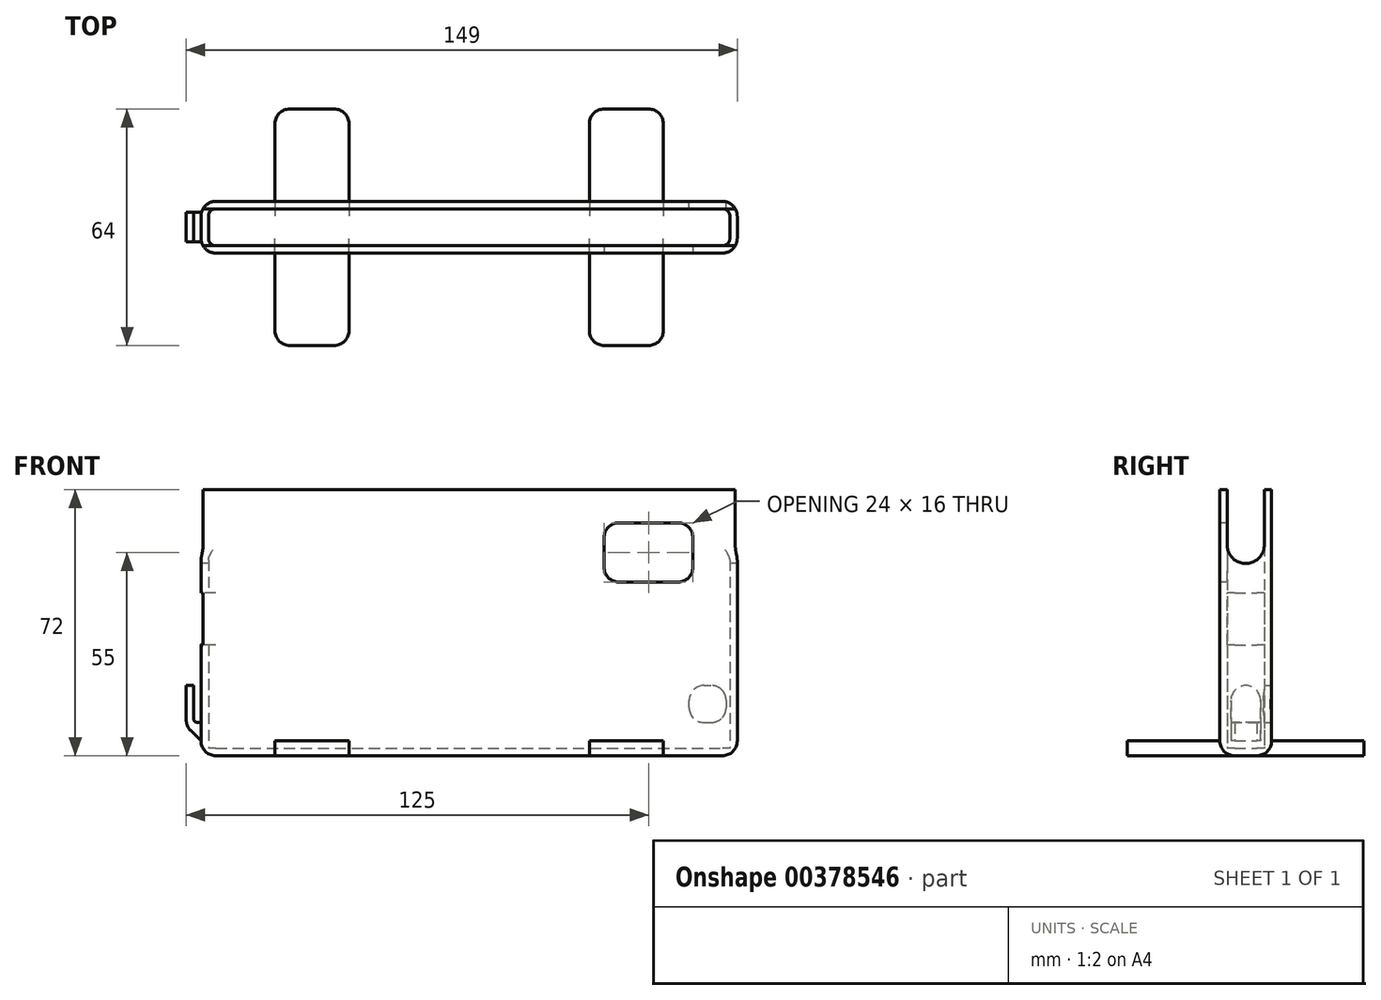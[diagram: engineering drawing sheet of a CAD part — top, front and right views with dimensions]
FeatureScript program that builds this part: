
annotation { "Feature Type Name" : "Feature", "Feature Type Description" : "" }
export const myFeature = defineFeature(function(context is Context, id is Id, definition is map)
    precondition{}
    {
        {
            var Q0;
            Q0=qCreatedBy(makeId("Top.planeOp"),FACE);
            var sketch = newSketch(context, id + "F0", { "sketchPlane" : qUnion([Q0])});
            skLineSegment(sketch, "E0.bottom", {"start": v(0, 0) * mm, "end": v(145, 0) * mm});
            skLineSegment(sketch, "E0.top", {"start": v(0, 14) * mm, "end": v(145, 14) * mm});
            skLineSegment(sketch, "E0.left", {"start": v(0, 0) * mm, "end": v(0, 14) * mm});
            skLineSegment(sketch, "E0.right", {"start": v(145, 0) * mm, "end": v(145, 14) * mm});
            skSolve(sketch);
        }
        {
            var Q0;
            Q0=qSketchRegion(id+"F0",true);
            extrude(context, id + "F1", {"entities" : qUnion([Q0]), "depth" : 2 * mm});
        }
        {
            var Q0;
            Q0=makeQuery(id+"F1.opExtrude","CAP_FACE",FACE,{"disambiguationData":[OSD([sQuery(id+"F0.wireOp",EDGE,"E0.bottom"),sQuery(id+"F0.wireOp",EDGE,"E0.top"),sQuery(id+"F0.wireOp",EDGE,"E0.left"),sQuery(id+"F0.wireOp",EDGE,"E0.right")])],"isStart":false});
            var sketch = newSketch(context, id + "F2", { "sketchPlane" : qUnion([Q0])});
            skLineSegment(sketch, "E1.0", {"start": v(0, 14) * mm, "end": v(145, 14) * mm});
            skLineSegment(sketch, "E1.1", {"start": v(0, 0) * mm, "end": v(0, 14) * mm});
            skLineSegment(sketch, "E1.2", {"start": v(0, 0) * mm, "end": v(145, 0) * mm});
            skLineSegment(sketch, "E1.3", {"start": v(145, 0) * mm, "end": v(145, 14) * mm});
            skLineSegment(sketch, "E2.0", {"start": v(2, 12) * mm, "end": v(143, 12) * mm});
            skLineSegment(sketch, "E2.1", {"start": v(2, 2) * mm, "end": v(2, 12) * mm});
            skLineSegment(sketch, "E2.2", {"start": v(2, 2) * mm, "end": v(143, 2) * mm});
            skLineSegment(sketch, "E2.3", {"start": v(143, 2) * mm, "end": v(143, 12) * mm});
            skSolve(sketch);
        }
        {
            var Q0;
            Q0=qSketchRegion(id+"F2",true);
            extrude(context, id + "F3", {"entities" : qUnion([Q0]), "operationType" : NewBodyOperationType.ADD, "depth" : 70 * mm});
        }
        {
            var Q0;
            Q0=makeQuery(id+"F3.opExtrude","SWEPT_EDGE",EDGE,{"disambiguationData":[OSD([sQuery(id+"F2.wireOp",EDGE,"E2.1"),sQuery(id+"F2.wireOp",EDGE,"E2.2")])]});
            var Q1;
            Q1=makeQuery(id+"F3.opExtrude","SWEPT_EDGE",EDGE,{"disambiguationData":[OSD([sQuery(id+"F2.wireOp",EDGE,"E2.0"),sQuery(id+"F2.wireOp",EDGE,"E2.1")])]});
            var Q2;
            Q2=makeQuery(id+"F3.opExtrude","SWEPT_EDGE",EDGE,{"disambiguationData":[OSD([sQuery(id+"F2.wireOp",EDGE,"E2.0"),sQuery(id+"F2.wireOp",EDGE,"E2.3")])]});
            var Q3;
            Q3=makeQuery(id+"F3.opExtrude","SWEPT_EDGE",EDGE,{"disambiguationData":[OSD([sQuery(id+"F2.wireOp",EDGE,"E2.2"),sQuery(id+"F2.wireOp",EDGE,"E2.3")])]});
            var Q4;
            Q4=makeQuery(id+"F3.opExtrude","CAP_EDGE",EDGE,{"disambiguationData":[OSD([sQuery(id+"F2.wireOp",EDGE,"E2.2")])],"isStart":true});
            var Q5;
            Q5=makeQuery(id+"F3.opExtrude","CAP_EDGE",EDGE,{"disambiguationData":[OSD([sQuery(id+"F2.wireOp",EDGE,"E2.3")])],"isStart":true});
            var Q6;
            Q6=makeQuery(id+"F3.opExtrude","CAP_EDGE",EDGE,{"disambiguationData":[OSD([sQuery(id+"F2.wireOp",EDGE,"E2.0")])],"isStart":true});
            var Q7;
            Q7=makeQuery(id+"F3.opExtrude","CAP_EDGE",EDGE,{"disambiguationData":[OSD([sQuery(id+"F2.wireOp",EDGE,"E2.1")])],"isStart":true});
            fillet(context, id + "F4", {"entities" : qUnion([Q0, Q1, Q2, Q3, Q4, Q5, Q6, Q7]), "radius" : 2 * mm, "tangentPropagation" : true, "allowEdgeOverflow" : false});
        }
        {
            var Q0;
            Q0=makeQuery(id+"F3.boolean.opBoolean","MERGE",EDGE,{"derivedFrom":[makeQuery(id+"F1.opExtrude","SWEPT_EDGE",EDGE,{"disambiguationData":[OSD([sQuery(id+"F0.wireOp",EDGE,"E0.bottom"),sQuery(id+"F0.wireOp",EDGE,"E0.left")])]}),makeQuery(id+"F3.opExtrude","SWEPT_EDGE",EDGE,{"disambiguationData":[OSD([sQuery(id+"F2.wireOp",EDGE,"E1.1"),sQuery(id+"F2.wireOp",EDGE,"E1.2")])]})]});
            var Q1;
            Q1=makeQuery(id+"F3.boolean.opBoolean","MERGE",EDGE,{"derivedFrom":[makeQuery(id+"F1.opExtrude","SWEPT_EDGE",EDGE,{"disambiguationData":[OSD([sQuery(id+"F0.wireOp",EDGE,"E0.top"),sQuery(id+"F0.wireOp",EDGE,"E0.left")])]}),makeQuery(id+"F3.opExtrude","SWEPT_EDGE",EDGE,{"disambiguationData":[OSD([sQuery(id+"F2.wireOp",EDGE,"E1.0"),sQuery(id+"F2.wireOp",EDGE,"E1.1")])]})]});
            var Q2;
            Q2=makeQuery(id+"F3.boolean.opBoolean","MERGE",EDGE,{"derivedFrom":[makeQuery(id+"F1.opExtrude","SWEPT_EDGE",EDGE,{"disambiguationData":[OSD([sQuery(id+"F0.wireOp",EDGE,"E0.top"),sQuery(id+"F0.wireOp",EDGE,"E0.right")])]}),makeQuery(id+"F3.opExtrude","SWEPT_EDGE",EDGE,{"disambiguationData":[OSD([sQuery(id+"F2.wireOp",EDGE,"E1.0"),sQuery(id+"F2.wireOp",EDGE,"E1.3")])]})]});
            var Q3;
            Q3=makeQuery(id+"F3.boolean.opBoolean","MERGE",EDGE,{"derivedFrom":[makeQuery(id+"F1.opExtrude","SWEPT_EDGE",EDGE,{"disambiguationData":[OSD([sQuery(id+"F0.wireOp",EDGE,"E0.bottom"),sQuery(id+"F0.wireOp",EDGE,"E0.right")])]}),makeQuery(id+"F3.opExtrude","SWEPT_EDGE",EDGE,{"disambiguationData":[OSD([sQuery(id+"F2.wireOp",EDGE,"E1.2"),sQuery(id+"F2.wireOp",EDGE,"E1.3")])]})]});
            var Q4;
            Q4=makeQuery(id+"F1.opExtrude","CAP_EDGE",EDGE,{"disambiguationData":[OSD([sQuery(id+"F0.wireOp",EDGE,"E0.bottom")])],"isStart":true});
            var Q5;
            Q5=makeQuery(id+"F1.opExtrude","CAP_EDGE",EDGE,{"disambiguationData":[OSD([sQuery(id+"F0.wireOp",EDGE,"E0.left")])],"isStart":true});
            var Q6;
            Q6=makeQuery(id+"F1.opExtrude","CAP_EDGE",EDGE,{"disambiguationData":[OSD([sQuery(id+"F0.wireOp",EDGE,"E0.top")])],"isStart":true});
            var Q7;
            Q7=makeQuery(id+"F1.opExtrude","CAP_EDGE",EDGE,{"disambiguationData":[OSD([sQuery(id+"F0.wireOp",EDGE,"E0.right")])],"isStart":true});
            fillet(context, id + "F5", {"entities" : qUnion([Q0, Q1, Q2, Q3, Q4, Q5, Q6, Q7]), "radius" : 4 * mm, "tangentPropagation" : true, "allowEdgeOverflow" : false});
        }
        {
            var Q0;
            Q0=makeQuery(id+"F3.boolean.opBoolean","MERGE",FACE,{"derivedFrom":[makeQuery(id+"F1.opExtrude","SWEPT_FACE",FACE,{"disambiguationData":[OSD([sQuery(id+"F0.wireOp",EDGE,"E0.left")])]}),makeQuery(id+"F3.opExtrude","SWEPT_FACE",FACE,{"disambiguationData":[OSD([sQuery(id+"F2.wireOp",EDGE,"E1.1")])]})]});
            var sketch = newSketch(context, id + "F6", { "sketchPlane" : qUnion([Q0])});
            skLineSegment(sketch, "E3", {"start": v(-7, 72) * mm, "end": v(-7, 57) * mm, "construction": true});
            skArc(sketch, "E4.0.startCap", {"start": v(-12, 72) * mm, "mid": v(-7, 77) * mm, "end": v(-2, 72) * mm});
            skArc(sketch, "E4.0.endCap", {"start": v(-2, 57) * mm, "mid": v(-7, 52) * mm, "end": v(-12, 57) * mm});
            skLineSegment(sketch, "E4.0.left", {"start": v(-2, 72) * mm, "end": v(-2, 57) * mm});
            skLineSegment(sketch, "E4.0.right", {"start": v(-12, 72) * mm, "end": v(-12, 57) * mm});
            skSolve(sketch);
        }
        {
            var Q0;
            Q0=qSketchRegion(id+"F6",true);
            extrude(context, id + "F7", {"entities" : qUnion([Q0]), "operationType" : NewBodyOperationType.REMOVE, "endBound" : BoundingType.THROUGH_ALL, "oppositeDirection" : true, "depth" : 25 * mm});
        }
        {
            var Q0;
            Q0=makeQuery(id+"F3.boolean.opBoolean","MERGE",FACE,{"derivedFrom":[makeQuery(id+"F1.opExtrude","SWEPT_FACE",FACE,{"disambiguationData":[OSD([sQuery(id+"F0.wireOp",EDGE,"E0.bottom")])]}),makeQuery(id+"F3.opExtrude","SWEPT_FACE",FACE,{"disambiguationData":[OSD([sQuery(id+"F2.wireOp",EDGE,"E1.2")])]})]});
            var sketch = newSketch(context, id + "F8", { "sketchPlane" : qUnion([Q0])});
            skLineSegment(sketch, "E5.bottom", {"start": v(113, 63) * mm, "end": v(129, 63) * mm});
            skLineSegment(sketch, "E5.top", {"start": v(113, 47) * mm, "end": v(129, 47) * mm});
            skLineSegment(sketch, "E5.left", {"start": v(109, 59) * mm, "end": v(109, 51) * mm});
            skLineSegment(sketch, "E5.right", {"start": v(133, 59) * mm, "end": v(133, 51) * mm});
            skPoint(sketch, "E6", {"position": v(109, 55) * mm});
            skPoint(sketch, "E7.visualSharp", {"position": v(109, 63) * mm});
            skArc(sketch, "E7.filletArc", {"start": v(113, 63) * mm, "mid": v(110.17, 61.83) * mm, "end": v(109, 59) * mm});
            skPoint(sketch, "E8.visualSharp", {"position": v(133, 63) * mm});
            skArc(sketch, "E8.filletArc", {"start": v(133, 59) * mm, "mid": v(131.83, 61.83) * mm, "end": v(129, 63) * mm});
            skPoint(sketch, "E9.visualSharp", {"position": v(133, 47) * mm});
            skArc(sketch, "E9.filletArc", {"start": v(129, 47) * mm, "mid": v(131.83, 48.17) * mm, "end": v(133, 51) * mm});
            skPoint(sketch, "E10.visualSharp", {"position": v(109, 47) * mm});
            skArc(sketch, "E10.filletArc", {"start": v(109, 51) * mm, "mid": v(110.17, 48.17) * mm, "end": v(113, 47) * mm});
            skPoint(sketch, "E11", {"position": v(121, 63) * mm});
            skSolve(sketch);
        }
        {
            var Q0;
            Q0=qSketchRegion(id+"F8",true);
            extrude(context, id + "F9", {"entities" : qUnion([Q0]), "operationType" : NewBodyOperationType.REMOVE, "endBound" : BoundingType.UP_TO_NEXT, "oppositeDirection" : true, "depth" : 25 * mm});
        }
        {
            var Q0;
            Q0=makeQuery(id+"F3.boolean.opBoolean","MERGE",FACE,{"derivedFrom":[makeQuery(id+"F1.opExtrude","SWEPT_FACE",FACE,{"disambiguationData":[OSD([sQuery(id+"F0.wireOp",EDGE,"E0.left")])]}),makeQuery(id+"F3.opExtrude","SWEPT_FACE",FACE,{"disambiguationData":[OSD([sQuery(id+"F2.wireOp",EDGE,"E1.1")])]})]});
            var sketch = newSketch(context, id + "F10", { "sketchPlane" : qUnion([Q0])});
            skLineSegment(sketch, "E12.bottom", {"start": v(-11, 19) * mm, "end": v(-3, 19) * mm});
            skLineSegment(sketch, "E12.top", {"start": v(-11, 4) * mm, "end": v(-3, 4) * mm});
            skLineSegment(sketch, "E12.left", {"start": v(-11, 19) * mm, "end": v(-11, 4) * mm});
            skLineSegment(sketch, "E12.right", {"start": v(-3, 19) * mm, "end": v(-3, 4) * mm});
            skPoint(sketch, "E13", {"position": v(-7, 4) * mm});
            skSolve(sketch);
        }
        {
            var Q0;
            Q0=qSketchRegion(id+"F10",true);
            extrude(context, id + "F11", {"entities" : qUnion([Q0]), "operationType" : NewBodyOperationType.ADD, "depth" : 4 * mm});
        }
        {
            var Q0;
            Q0=makeQuery(id+"F11.opExtrude","CAP_EDGE",EDGE,{"disambiguationData":[OSD([sQuery(id+"F10.wireOp",EDGE,"E12.top")])],"isStart":false});
            chamfer(context, id + "F12", {"entities" : qUnion([Q0]), "width" : 4 * mm, "tangentPropagation" : true});
        }
        {
            var Q0;
            Q0=makeQuery(id+"F11.opExtrude","SWEPT_FACE",FACE,{"disambiguationData":[OSD([sQuery(id+"F10.wireOp",EDGE,"E12.bottom")])]});
            var sketch = newSketch(context, id + "F13", { "sketchPlane" : qUnion([Q0])});
            skLineSegment(sketch, "E14.bottom", {"start": v(-2, 11) * mm, "end": v(0, 11) * mm});
            skLineSegment(sketch, "E14.top", {"start": v(-2, 3) * mm, "end": v(0, 3) * mm});
            skLineSegment(sketch, "E14.left", {"start": v(0, 3) * mm, "end": v(0, 11) * mm});
            skLineSegment(sketch, "E14.right", {"start": v(-2, 3) * mm, "end": v(-2, 11) * mm});
            skSolve(sketch);
        }
        {
            var Q0;
            Q0=qSketchRegion(id+"F13",true);
            extrude(context, id + "F14", {"entities" : qUnion([Q0]), "operationType" : NewBodyOperationType.REMOVE, "oppositeDirection" : true, "depth" : 10 * mm});
        }
        {
            var Q0;
            Q0=makeQuery(id+"F11.opExtrude","SWEPT_EDGE",EDGE,{"disambiguationData":[OSD([sQuery(id+"F10.wireOp",EDGE,"E12.bottom"),sQuery(id+"F10.wireOp",EDGE,"E12.left")])]});
            var Q1;
            Q1=makeQuery(id+"F11.opExtrude","SWEPT_EDGE",EDGE,{"disambiguationData":[OSD([sQuery(id+"F10.wireOp",EDGE,"E12.bottom"),sQuery(id+"F10.wireOp",EDGE,"E12.right")])]});
            var Q2;
            {var subQ0=sQuery(id+"F10.wireOp",EDGE,"E12.top");Q2=makeQuery(id+"F12.opChamfer","BLEND_EDGE",EDGE,{"blendedFrom":[makeQuery(id+"F11.opExtrude","CAP_EDGE",EDGE,{"disambiguationData":[OSD([subQ0])],"isStart":false}),makeQuery(id+"F11.opExtrude","CAP_FACE",FACE,{"disambiguationData":[OSD([sQuery(id+"F10.wireOp",EDGE,"E12.bottom"),subQ0,sQuery(id+"F10.wireOp",EDGE,"E12.left"),sQuery(id+"F10.wireOp",EDGE,"E12.right")])],"isStart":false})],"blendedInto":[makeQuery(id+"F11.opExtrude","CAP_FACE",FACE,{"disambiguationData":[OSD([sQuery(id+"F10.wireOp",EDGE,"E12.bottom"),subQ0,sQuery(id+"F10.wireOp",EDGE,"E12.left"),sQuery(id+"F10.wireOp",EDGE,"E12.right")])],"isStart":false})]});}
            fillet(context, id + "F15", {"entities" : qUnion([Q0, Q1, Q2]), "radius" : 4 * mm, "tangentPropagation" : true, "allowEdgeOverflow" : false});
        }
        {
            var Q0;
            Q0=makeQuery(id+"F14.boolean.opBoolean","COPY",EDGE,{"derivedFrom":makeQuery(id+"F14.opExtrude","CAP_EDGE",EDGE,{"disambiguationData":[OSD([sQuery(id+"F13.wireOp",EDGE,"E14.right")])],"isStart":false})});
            fillet(context, id + "F16", {"entities" : qUnion([Q0]), "radius" : 1 * mm, "tangentPropagation" : true, "allowEdgeOverflow" : false});
        }
        {
            var Q0;
            Q0=makeQuery(id+"F3.boolean.opBoolean","MERGE",FACE,{"derivedFrom":[makeQuery(id+"F1.opExtrude","SWEPT_FACE",FACE,{"disambiguationData":[OSD([sQuery(id+"F0.wireOp",EDGE,"E0.top")])]}),makeQuery(id+"F3.opExtrude","SWEPT_FACE",FACE,{"disambiguationData":[OSD([sQuery(id+"F2.wireOp",EDGE,"E1.0")])]})]});
            var sketch = newSketch(context, id + "F17", { "sketchPlane" : qUnion([Q0])});
            skLineSegment(sketch, "E15.bottom", {"start": v(-138, 19) * mm, "end": v(-136, 19) * mm});
            skLineSegment(sketch, "E15.top", {"start": v(-138, 9) * mm, "end": v(-136, 9) * mm});
            skLineSegment(sketch, "E15.left", {"start": v(-142, 15) * mm, "end": v(-142, 13) * mm});
            skLineSegment(sketch, "E15.right", {"start": v(-132, 15) * mm, "end": v(-132, 13) * mm});
            skPoint(sketch, "E16.visualSharp", {"position": v(-142, 19) * mm});
            skArc(sketch, "E16.filletArc", {"start": v(-138, 19) * mm, "mid": v(-140.83, 17.83) * mm, "end": v(-142, 15) * mm});
            skPoint(sketch, "E17.visualSharp", {"position": v(-132, 19) * mm});
            skArc(sketch, "E17.filletArc", {"start": v(-132, 15) * mm, "mid": v(-133.17, 17.83) * mm, "end": v(-136, 19) * mm});
            skPoint(sketch, "E18.visualSharp", {"position": v(-132, 9) * mm});
            skArc(sketch, "E18.filletArc", {"start": v(-136, 9) * mm, "mid": v(-133.17, 10.17) * mm, "end": v(-132, 13) * mm});
            skPoint(sketch, "E19.visualSharp", {"position": v(-142, 9) * mm});
            skArc(sketch, "E19.filletArc", {"start": v(-142, 13) * mm, "mid": v(-140.83, 10.17) * mm, "end": v(-138, 9) * mm});
            skPoint(sketch, "E20", {"position": v(-137, 19) * mm});
            skPoint(sketch, "E21", {"position": v(-132, 14) * mm});
            skSolve(sketch);
        }
        {
            var Q0;
            Q0=qSketchRegion(id+"F17",true);
            extrude(context, id + "F18", {"entities" : qUnion([Q0]), "operationType" : NewBodyOperationType.REMOVE, "endBound" : BoundingType.UP_TO_NEXT, "oppositeDirection" : true, "depth" : 25 * mm});
        }
        {
            var Q0;
            Q0=makeQuery(id+"F3.boolean.opBoolean","MERGE",FACE,{"derivedFrom":[makeQuery(id+"F1.opExtrude","SWEPT_FACE",FACE,{"disambiguationData":[OSD([sQuery(id+"F0.wireOp",EDGE,"E0.left")])]}),makeQuery(id+"F3.opExtrude","SWEPT_FACE",FACE,{"disambiguationData":[OSD([sQuery(id+"F2.wireOp",EDGE,"E1.1")])]})]});
            var sketch = newSketch(context, id + "F19", { "sketchPlane" : qUnion([Q0])});
            skLineSegment(sketch, "E22.bottom", {"start": v(-2, 44) * mm, "end": v(-12, 44) * mm});
            skLineSegment(sketch, "E22.top", {"start": v(-2, 30) * mm, "end": v(-12, 30) * mm});
            skLineSegment(sketch, "E22.left", {"start": v(-2, 44) * mm, "end": v(-2, 30) * mm});
            skLineSegment(sketch, "E22.right", {"start": v(-12, 44) * mm, "end": v(-12, 30) * mm});
            skPoint(sketch, "E22.middle", {"position": v(-7, 37) * mm});
            skLineSegment(sketch, "E23", {"start": v(-10, 31) * mm, "end": v(-4, 31) * mm, "construction": true});
            skPoint(sketch, "E24", {"position": v(-7, 31) * mm});
            skSolve(sketch);
        }
        {
            var Q0;
            Q0=qSketchRegion(id+"F19",true);
            extrude(context, id + "F20", {"entities" : qUnion([Q0]), "operationType" : NewBodyOperationType.REMOVE, "endBound" : BoundingType.UP_TO_NEXT, "oppositeDirection" : true, "depth" : 25 * mm});
        }
        {
            var Q0;
            Q0=makeQuery(id+"F3.boolean.opBoolean","MERGE",FACE,{"derivedFrom":[makeQuery(id+"F1.opExtrude","SWEPT_FACE",FACE,{"disambiguationData":[OSD([sQuery(id+"F0.wireOp",EDGE,"E0.top")])]}),makeQuery(id+"F3.opExtrude","SWEPT_FACE",FACE,{"disambiguationData":[OSD([sQuery(id+"F2.wireOp",EDGE,"E1.0")])]})]});
            var sketch = newSketch(context, id + "F21", { "sketchPlane" : qUnion([Q0])});
            skLineSegment(sketch, "E25.bottom", {"start": v(-125, 4) * mm, "end": v(-105, 4) * mm});
            skLineSegment(sketch, "E25.top", {"start": v(-125, 0) * mm, "end": v(-105, 0) * mm});
            skLineSegment(sketch, "E25.left", {"start": v(-125, 4) * mm, "end": v(-125, 0) * mm});
            skLineSegment(sketch, "E25.right", {"start": v(-105, 4) * mm, "end": v(-105, 0) * mm});
            skLineSegment(sketch, "E26.bottom", {"start": v(-40, 4) * mm, "end": v(-20, 4) * mm});
            skLineSegment(sketch, "E26.top", {"start": v(-40, 0) * mm, "end": v(-20, 0) * mm});
            skLineSegment(sketch, "E26.left", {"start": v(-40, 4) * mm, "end": v(-40, 0) * mm});
            skLineSegment(sketch, "E26.right", {"start": v(-20, 4) * mm, "end": v(-20, 0) * mm});
            skSolve(sketch);
        }
        {
            var Q0;
            Q0=qSketchRegion(id+"F21",true);
            var Q1;
            Q1=makeQuery(id+"F1.opExtrude","SWEPT_BODY",BODY,{"disambiguationData":[OSD([sQuery(id+"F0.wireOp",EDGE,"E0.bottom"),sQuery(id+"F0.wireOp",EDGE,"E0.top"),sQuery(id+"F0.wireOp",EDGE,"E0.left"),sQuery(id+"F0.wireOp",EDGE,"E0.right")])]});
            extrude(context, id + "F22", {"entities" : qUnion([Q0]), "operationType" : NewBodyOperationType.ADD, "depth" : 25 * mm, "hasSecondDirection" : true, "secondDirectionBound" : SecondDirectionBoundingType.UP_TO_BODY, "secondDirectionOppositeDirection" : true, "secondDirectionBoundEntityBody" : qUnion([Q1]), "secondDirectionDepth" : 25 * mm});
        }
        {
            var Q0;
            Q0=makeQuery(id+"F3.boolean.opBoolean","MERGE",FACE,{"derivedFrom":[makeQuery(id+"F1.opExtrude","SWEPT_FACE",FACE,{"disambiguationData":[OSD([sQuery(id+"F0.wireOp",EDGE,"E0.bottom")])]}),makeQuery(id+"F3.opExtrude","SWEPT_FACE",FACE,{"disambiguationData":[OSD([sQuery(id+"F2.wireOp",EDGE,"E1.2")])]})]});
            var sketch = newSketch(context, id + "F23", { "sketchPlane" : qUnion([Q0])});
            skLineSegment(sketch, "E27.bottom", {"start": v(20, 4) * mm, "end": v(40, 4) * mm});
            skLineSegment(sketch, "E27.top", {"start": v(20, 0) * mm, "end": v(40, 0) * mm});
            skLineSegment(sketch, "E27.left", {"start": v(20, 4) * mm, "end": v(20, 0) * mm});
            skLineSegment(sketch, "E27.right", {"start": v(40, 4) * mm, "end": v(40, 0) * mm});
            skLineSegment(sketch, "E28.bottom", {"start": v(105, 4) * mm, "end": v(125, 4) * mm});
            skLineSegment(sketch, "E28.top", {"start": v(105, 0) * mm, "end": v(125, 0) * mm});
            skLineSegment(sketch, "E28.left", {"start": v(105, 4) * mm, "end": v(105, 0) * mm});
            skLineSegment(sketch, "E28.right", {"start": v(125, 4) * mm, "end": v(125, 0) * mm});
            skSolve(sketch);
        }
        {
            var Q0;
            Q0=qSketchRegion(id+"F23",true);
            var Q1;
            Q1=makeQuery(id+"F1.opExtrude","SWEPT_BODY",BODY,{"disambiguationData":[OSD([sQuery(id+"F0.wireOp",EDGE,"E0.bottom"),sQuery(id+"F0.wireOp",EDGE,"E0.top"),sQuery(id+"F0.wireOp",EDGE,"E0.left"),sQuery(id+"F0.wireOp",EDGE,"E0.right")])]});
            extrude(context, id + "F24", {"entities" : qUnion([Q0]), "operationType" : NewBodyOperationType.ADD, "depth" : 25 * mm, "hasSecondDirection" : true, "secondDirectionBound" : SecondDirectionBoundingType.UP_TO_BODY, "secondDirectionOppositeDirection" : true, "secondDirectionBoundEntityBody" : qUnion([Q1]), "secondDirectionDepth" : 25 * mm});
        }
        {
            var Q0;
            {var subQ0=sQuery(id+"F23.wireOp",EDGE,"E27.left");Q0=makeQuery(id+"F24.opExtrude","CAP_EDGE",EDGE,{"disambiguationData":[OSD([subQ0]),topologyDisambiguationEdgeConnected([makeQuery(id+"F23.imprint","IMPRINT",EDGE,{"derivedFrom":sQuery(id+"F23.wireOp",EDGE,"E27.bottom")})])],"isStart":false});}
            var Q1;
            {var subQ0=sQuery(id+"F23.wireOp",EDGE,"E27.right");Q1=makeQuery(id+"F24.opExtrude","CAP_EDGE",EDGE,{"disambiguationData":[OSD([subQ0]),topologyDisambiguationEdgeConnected([makeQuery(id+"F23.imprint","IMPRINT",EDGE,{"derivedFrom":sQuery(id+"F23.wireOp",EDGE,"E27.bottom")})])],"isStart":false});}
            var Q2;
            {var subQ0=sQuery(id+"F23.wireOp",EDGE,"E28.left");Q2=makeQuery(id+"F24.opExtrude","CAP_EDGE",EDGE,{"disambiguationData":[OSD([subQ0]),topologyDisambiguationEdgeConnected([makeQuery(id+"F23.imprint","IMPRINT",EDGE,{"derivedFrom":sQuery(id+"F23.wireOp",EDGE,"E28.bottom")})])],"isStart":false});}
            var Q3;
            {var subQ0=sQuery(id+"F23.wireOp",EDGE,"E28.right");Q3=makeQuery(id+"F24.opExtrude","CAP_EDGE",EDGE,{"disambiguationData":[OSD([subQ0]),topologyDisambiguationEdgeConnected([makeQuery(id+"F23.imprint","IMPRINT",EDGE,{"derivedFrom":sQuery(id+"F23.wireOp",EDGE,"E28.bottom")})])],"isStart":false});}
            var Q4;
            {var subQ0=sQuery(id+"F21.wireOp",EDGE,"E26.right");Q4=makeQuery(id+"F22.opExtrude","CAP_EDGE",EDGE,{"disambiguationData":[OSD([subQ0]),topologyDisambiguationEdgeConnected([makeQuery(id+"F21.imprint","IMPRINT",EDGE,{"derivedFrom":sQuery(id+"F21.wireOp",EDGE,"E26.bottom")})])],"isStart":false});}
            var Q5;
            {var subQ0=sQuery(id+"F21.wireOp",EDGE,"E26.left");Q5=makeQuery(id+"F22.opExtrude","CAP_EDGE",EDGE,{"disambiguationData":[OSD([subQ0]),topologyDisambiguationEdgeConnected([makeQuery(id+"F21.imprint","IMPRINT",EDGE,{"derivedFrom":sQuery(id+"F21.wireOp",EDGE,"E26.bottom")})])],"isStart":false});}
            var Q6;
            {var subQ0=sQuery(id+"F21.wireOp",EDGE,"E25.right");Q6=makeQuery(id+"F22.opExtrude","CAP_EDGE",EDGE,{"disambiguationData":[OSD([subQ0]),topologyDisambiguationEdgeConnected([makeQuery(id+"F21.imprint","IMPRINT",EDGE,{"derivedFrom":sQuery(id+"F21.wireOp",EDGE,"E25.bottom")})])],"isStart":false});}
            var Q7;
            {var subQ0=sQuery(id+"F21.wireOp",EDGE,"E25.left");Q7=makeQuery(id+"F22.opExtrude","CAP_EDGE",EDGE,{"disambiguationData":[OSD([subQ0]),topologyDisambiguationEdgeConnected([makeQuery(id+"F21.imprint","IMPRINT",EDGE,{"derivedFrom":sQuery(id+"F21.wireOp",EDGE,"E25.bottom")})])],"isStart":false});}
            fillet(context, id + "F25", {"entities" : qUnion([Q0, Q1, Q2, Q3, Q4, Q5, Q6, Q7]), "radius" : 4 * mm, "tangentPropagation" : true, "allowEdgeOverflow" : false});
        }
    });
